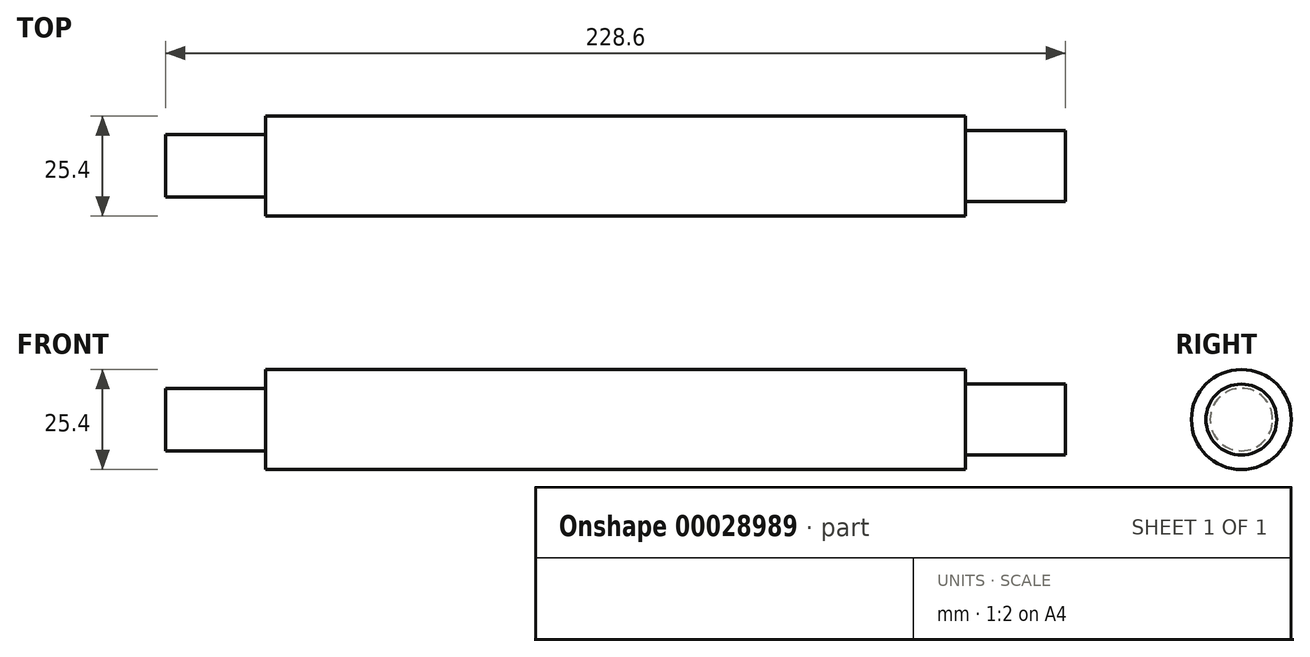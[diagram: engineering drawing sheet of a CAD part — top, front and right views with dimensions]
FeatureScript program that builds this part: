
annotation { "Feature Type Name" : "Feature", "Feature Type Description" : "" }
export const myFeature = defineFeature(function(context is Context, id is Id, definition is map)
    precondition{}
    {
        {
            var Q0;
            Q0=qCreatedBy(makeId("Right.planeOp"),FACE);
            var sketch = newSketch(context, id + "F0", { "sketchPlane" : qUnion([Q0])});
            skCircle(sketch, "E0", {"center": v(0, 0) * mm, "radius": 12.7 * mm});
            skSolve(sketch);
        }
        {
            var Q0;
            Q0 = qSketchRegion(id + "F0", true);
            extrude(context, id + "F1", {"entities" : qUnion([Q0]), "endBound" : BoundingType.SYMMETRIC, "depth" : 177.8 * mm});
        }
        {
            var Q0;
            Q0=makeQuery(id+"F1.opExtrude","CAP_FACE",FACE,{"disambiguationData":[OSD([sQuery(id+"F0.wireOp",EDGE,"E0")])],"isStart":false});
            var sketch = newSketch(context, id + "F2", { "sketchPlane" : qUnion([Q0])});
            skCircle(sketch, "E1", {"center": v(0, 0) * mm, "radius": 9 * mm});
            skSolve(sketch);
        }
        {
            var Q0;
            Q0 = qSketchRegion(id + "F2", true);
            extrude(context, id + "F3", {"entities" : qUnion([Q0]), "depth" : 25.4 * mm});
        }
        {
            var Q0;
            Q0=makeQuery(id+"F1.opExtrude","CAP_FACE",FACE,{"disambiguationData":[OSD([sQuery(id+"F0.wireOp",EDGE,"E0")])],"isStart":true});
            var sketch = newSketch(context, id + "F4", { "sketchPlane" : qUnion([Q0])});
            skCircle(sketch, "E2", {"center": v(0, 0) * mm, "radius": 7.94 * mm});
            skSolve(sketch);
        }
        {
            var Q0;
            Q0 = qSketchRegion(id + "F4", true);
            extrude(context, id + "F5", {"entities" : qUnion([Q0]), "operationType" : NewBodyOperationType.ADD, "depth" : 25.4 * mm});
        }
    });
